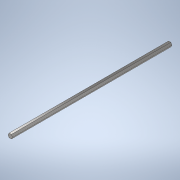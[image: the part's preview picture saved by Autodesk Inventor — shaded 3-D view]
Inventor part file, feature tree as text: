
AUTODESK INVENTOR PART (.ipt)
format: ipt  version: 2020 (Build 240168000, 168)  size: 104,448 bytes
history: native  units: in
note: dims shown in document units (in); Inventor stores cm internally (conversion verified against a paired STEP export)
features: extrude x1, sketch x1
ambient origin geometry x8: Origin, YZ Plane, XZ Plane, XY Plane, X Axis, Y Axis, Z Axis, Center Point
bodies: Solid1 (feature_tree)
feature tree (2):
  extrude  "Extrusion1"  Depth=20.0in TaperAngle=0.0deg
  sketch  "Sketch1"  dims[d0=0.5in d1=20.0in d2=0.0in]
